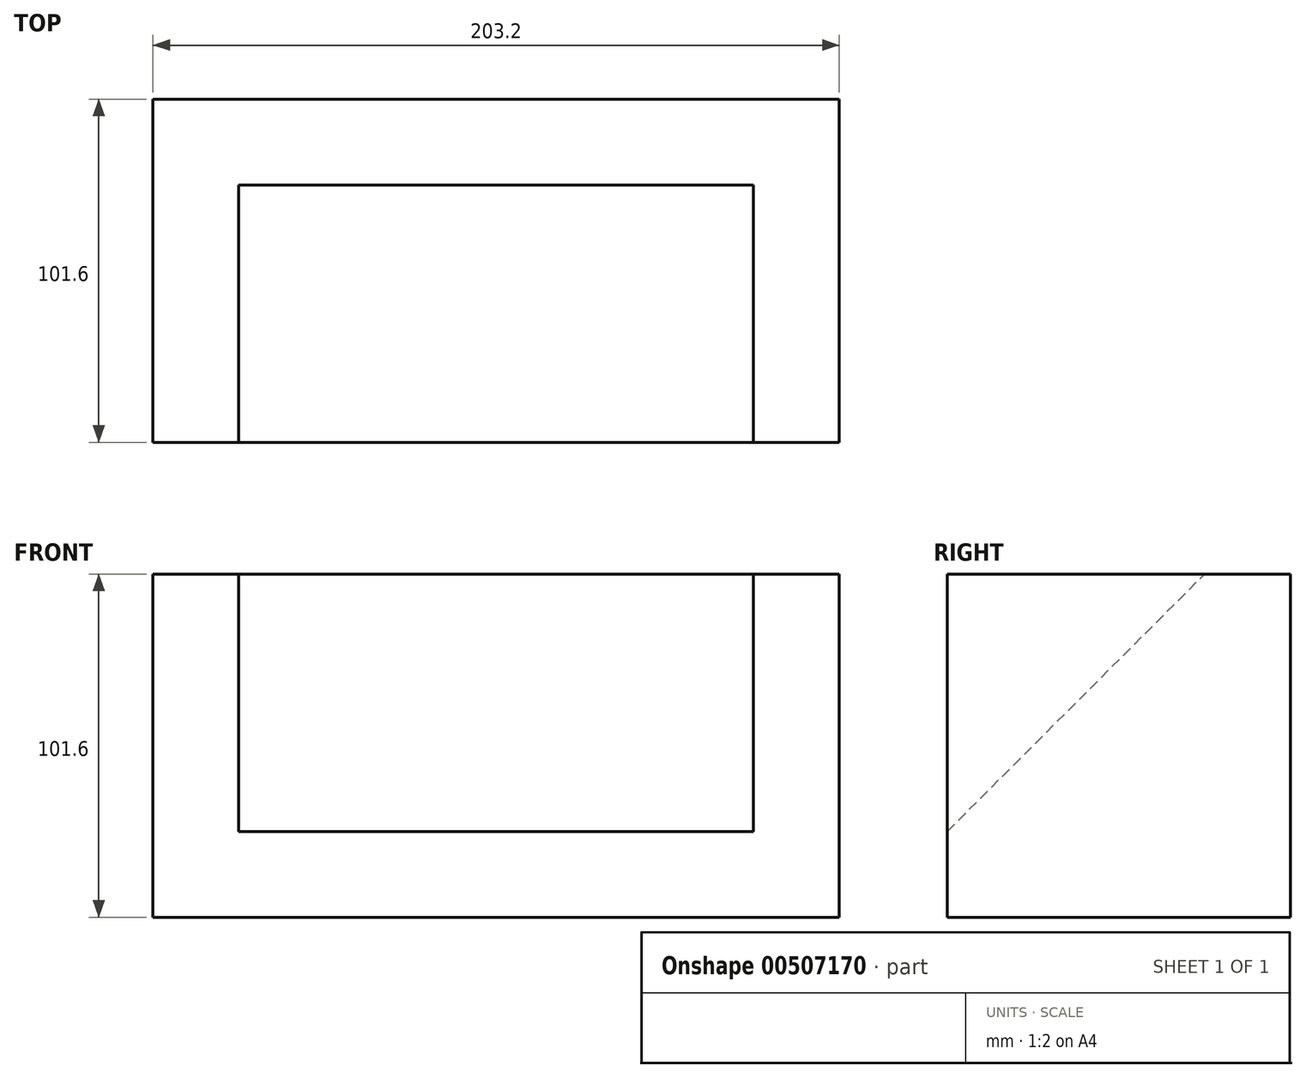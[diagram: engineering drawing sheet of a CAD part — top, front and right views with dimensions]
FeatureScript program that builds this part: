
annotation { "Feature Type Name" : "Feature", "Feature Type Description" : "" }
export const myFeature = defineFeature(function(context is Context, id is Id, definition is map)
    precondition{}
    {
        {
            var Q0;
            Q0=qCreatedBy(makeId("Front.planeOp"),FACE);
            var sketch = newSketch(context, id + "F0", { "sketchPlane" : qUnion([Q0])});
            skLineSegment(sketch, "E0.bottom", {"start": v(-101.6, 50.8) * mm, "end": v(101.6, 50.8) * mm});
            skLineSegment(sketch, "E0.top", {"start": v(-101.6, -50.8) * mm, "end": v(101.6, -50.8) * mm});
            skLineSegment(sketch, "E0.left", {"start": v(-101.6, 50.8) * mm, "end": v(-101.6, -50.8) * mm});
            skLineSegment(sketch, "E0.right", {"start": v(101.6, 50.8) * mm, "end": v(101.6, -50.8) * mm});
            skSolve(sketch);
        }
        {
            var Q0;
            Q0=qSketchRegion(id+"F0",true);
            extrude(context, id + "F1", {"entities" : qUnion([Q0]), "depth" : 101.6 * mm});
        }
        {
            var Q0;
            Q0=makeQuery(id+"F1.opExtrude","SWEPT_FACE",FACE,{"disambiguationData":[OSD([sQuery(id+"F0.wireOp",EDGE,"E0.bottom")])]});
            var sketch = newSketch(context, id + "F2", { "sketchPlane" : qUnion([Q0])});
            skLineSegment(sketch, "E1.bottom", {"start": v(-76.2, -101.6) * mm, "end": v(76.2, -101.6) * mm});
            skLineSegment(sketch, "E1.top", {"start": v(-76.2, -25.4) * mm, "end": v(76.2, -25.4) * mm});
            skLineSegment(sketch, "E1.left", {"start": v(-76.2, -101.6) * mm, "end": v(-76.2, -25.4) * mm});
            skLineSegment(sketch, "E1.right", {"start": v(76.2, -101.6) * mm, "end": v(76.2, -25.4) * mm});
            skSolve(sketch);
        }
        {
            var Q0;
            Q0 = qSketchRegion(id + "F2", true);
            extrude(context, id + "F3", {"entities" : qUnion([Q0]), "operationType" : NewBodyOperationType.REMOVE, "oppositeDirection" : true, "depth" : 76.2 * mm});
        }
        {
            var Q0;
            Q0=makeQuery(id+"F3.boolean.opBoolean","COPY",FACE,{"derivedFrom":makeQuery(id+"F3.opExtrude","SWEPT_FACE",FACE,{"disambiguationData":[OSD([sQuery(id+"F2.wireOp",EDGE,"E1.left")])]})});
            var sketch = newSketch(context, id + "F4", { "sketchPlane" : qUnion([Q0])});
            skLineSegment(sketch, "E2", {"start": v(-101.6, -25.4) * mm, "end": v(-25.4, 50.8) * mm});
            skLineSegment(sketch, "E3", {"start": v(-25.4, 50.8) * mm, "end": v(-25.4, -25.4) * mm});
            skLineSegment(sketch, "E4", {"start": v(-25.4, -25.4) * mm, "end": v(-101.6, -25.4) * mm});
            skSolve(sketch);
        }
        {
            var Q0;
            Q0 = qSketchRegion(id + "F4", true);
            extrude(context, id + "F5", {"entities" : qUnion([Q0]), "operationType" : NewBodyOperationType.ADD, "depth" : 152.4 * mm});
        }
    });
